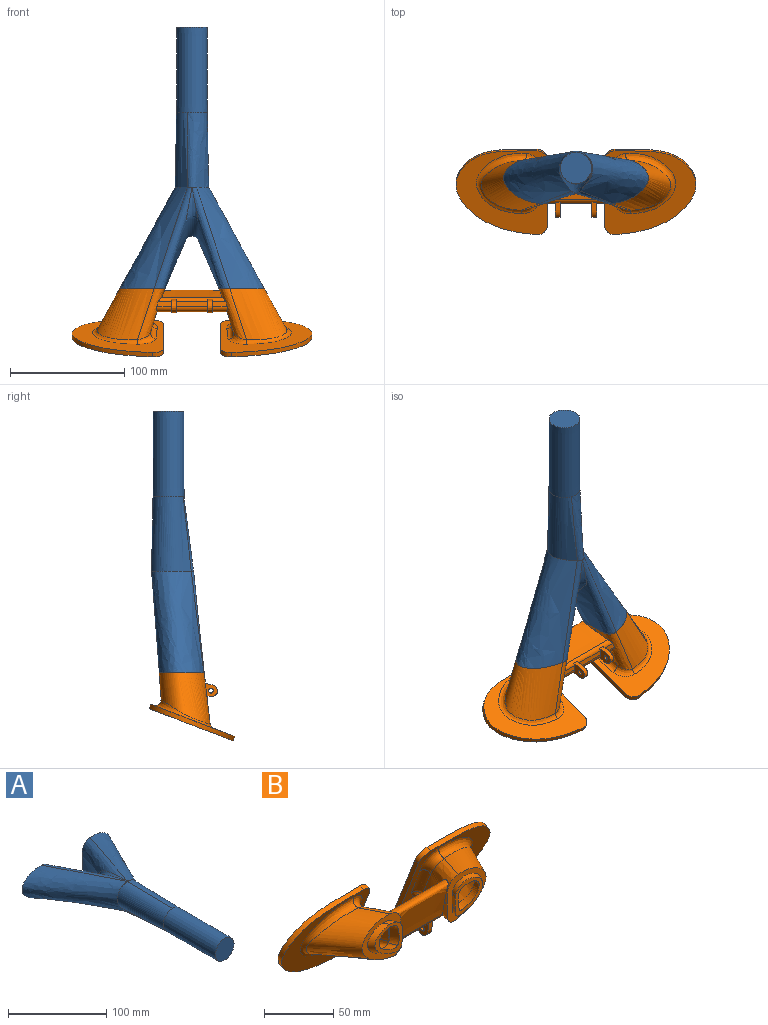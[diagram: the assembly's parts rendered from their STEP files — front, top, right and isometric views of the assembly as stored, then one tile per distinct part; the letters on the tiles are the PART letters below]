
ASSEMBLY  parts=2 mates=1
PART A: 30 faces, bbox 138.5x252.4x49 mm
  f0: bspline ~4.21x1.51mm, area 0.9mm2, adj f2,f13,f14,f15
  f1: plane 8.5x1.11mm, normal (0,-1,0), area 1.6mm2, adj f5,f14
  f2: plane 6.41x0.91mm, normal (0,-1,0), area 1.4mm2, adj f0,f5,f6,f13
  f3: plane 17.1x17.1mm, normal (0,1,0), area 229.7mm2, adj f4
  f4: cone r=5.55mm half-angle=2.5deg, axis (0,-1,0), area 3103.6mm2, adj f3,f5,f6
  f5: bspline ~65x21.5mm, area 1779.1mm2, adj f1,f2,f4,f6,f8,f10
  f6: bspline ~65x19.47mm, area 1298.2mm2, adj f2,f4,f5,f7,f9,f10
  f7: plane 8.48x1.1mm, normal (0,-1,0), area 1.6mm2, adj f6,f12
  f8: plane 4.77x4.68mm, normal (0,1,0), area 1mm2, adj f5,f14
  f9: plane 4.77x4.68mm, normal (0,1,0), area 1mm2, adj f6,f12
  f10: plane 15.72x8.94mm, normal (0,1,0), area 6.3mm2, adj f5,f6,f11,f12,f14,f15
  f11: bspline ~96.65x53.47mm, area 2584.8mm2, adj f10,f12,f13,f15,f17
  f12: bspline ~98.61x60.45mm, area 3778.7mm2, adj f7,f9,f10,f11,f13,f17
  f13: bspline ~4.27x1.64mm, area 0.9mm2, adj f0,f2,f11,f12
  f14: bspline ~98.61x60.44mm, area 3778.7mm2, adj f0,f1,f8,f10,f15,f16
  f15: bspline ~108.27x58.9mm, area 2584.8mm2, adj f0,f10,f11,f14,f16
  f16: plane 39.79x39.48mm, normal (0,1,0), area 579.5mm2, adj f14,f15,f19,f26
  f17: plane 39.77x39.46mm, normal (0,1,0), area 579.6mm2, adj f11,f12,f18,f24
  f18: bspline ~101.02x51.7mm, area 3195.4mm2, adj f17,f22,f24,f25,f29
  f19: bspline ~101.02x51.7mm, area 3193.5mm2, adj f16,f22,f26,f27,f29
  f20: plane 27.05x27.05mm, normal (0,-1,0), area 574.7mm2, adj f21
  f21: cone r=13.53mm half-angle=0deg, axis (0,1,0), area 6379.4mm2, adj f20,f22,f23
  f22: bspline ~65x37.02mm, area 3332mm2, adj f18,f19,f21,f23,f26
  f23: bspline ~65.77x34.91mm, area 2741.8mm2, adj f21,f22,f24,f27,f28
  f24: bspline ~111.93x71.83mm, area 5752.2mm2, adj f17,f18,f23,f25
  f25: cylinder r=11.3mm len=2.76mm, axis (0.37,0.92,-0.07), area 1.7mm2, adj f18,f24,f28
  f26: bspline ~101.1x66.24mm, area 5752.5mm2, adj f16,f19,f22,f27
  f27: cylinder r=11.33mm len=2.86mm, axis (0.37,-0.92,0.07), area 1.7mm2, adj f19,f23,f26,f28
  f28: bspline ~3.24x0.81mm, area 0.4mm2, adj f23,f25,f27
  f29: bspline ~46.56x37.54mm, area 612.9mm2, adj f18,f19
PART B: 80 faces, bbox 214.9x78.1x79.1 mm
  f0: plane 38.66x35.69mm, normal (0,-0.93,-0.36), area 1179.4mm2, adj f1,f2
  f1: bspline ~49.35x47.8mm, area 2433.5mm2, adj f0,f2,f71
  f2: bspline ~48.81x34.27mm, area 1258.8mm2, adj f0,f1,f70,f71,f72,f73
  f3: plane 26.69x25.63mm, normal (0,1,0), area 146.6mm2, adj f4,f70,f71,f73
  f4: bspline ~25.62x20.83mm, area 557.8mm2, adj f3,f5,f72
  f5: plane 29.75x29.28mm, normal (0,-1,0), area 261.4mm2, adj f4,f68,f69
  f6: plane 4.32x1.28mm, normal (0,1,0), area 0.7mm2, adj f12,f14
  f7: plane 38.66x35.66mm, normal (0,-0.93,-0.36), area 1178.6mm2, adj f8,f9,f15
  f8: bspline ~49.35x47.8mm, area 2433.5mm2, adj f7,f9,f11
  f9: bspline ~48.81x34.27mm, area 1258.8mm2, adj f7,f8,f11,f12,f15
  f10: plane 28.48x27.41mm, normal (0,1,0), area 74.5mm2, adj f11,f12,f13,f14
  f11: bspline ~30.27x28.42mm, area 140.7mm2, adj f8,f9,f10,f12
  f12: bspline ~24.9x17.72mm, area 121.3mm2, adj f6,f9,f10,f11,f13,f14
  f13: bspline ~24.99x23.73mm, area 473.2mm2, adj f10,f12,f14,f66
  f14: bspline ~19.22x10.5mm, area 154.8mm2, adj f6,f10,f12,f13,f66
  f15: bspline ~4.07x0.5mm, area 0mm2, adj f7,f9
  f16: cylinder r=4mm len=59.09mm, axis (-1,0,0), area 279.3mm2, adj f18,f19,f20,f21,f36,f37,f38,f39
  f17: cylinder r=4mm len=61.72mm, axis (-1,0,0), area 431.6mm2, adj f18,f19,f20,f21,f36,f37,f38,f39
  f18: plane 12.86x4.19mm, normal (0,-0.09,-1), area 51.3mm2, adj f16,f17,f20,f42
  f19: plane 12.86x4.19mm, normal (0,-0.09,-1), area 51.3mm2, adj f16,f17,f21,f39
  f20: bspline ~55.24x45.18mm, area 1346.7mm2, adj f16,f17,f18,f22,f37,f54,f55,f56
  f21: bspline ~55.24x45.18mm, area 1346.8mm2, adj f16,f17,f19,f29,f37,f53,f59,f60
  f22: bspline ~55.29x52.17mm, area 2946.7mm2, adj f20,f54,f57
  f23: cylinder r=9mm len=9.84mm, axis (0,-0.93,-0.36), area 59.6mm2, adj f24,f26,f27,f28
  f24: extruded ~74.76x70.56mm, area 712.1mm2, adj f23,f25,f27,f28
  f25: cylinder r=9mm len=9.84mm, axis (0,-0.93,-0.36), area 57.9mm2, adj f24,f26,f27,f28
  f26: plane 57.99x25.44mm, normal (1,0,0), area 242.3mm2, adj f23,f25,f27,f28
  f27: plane 80.61x73.97mm, normal (0,0.93,0.36), area 5149.4mm2, adj f23,f24,f25,f26
  f28: plane 80.61x73.97mm, normal (0,-0.93,-0.36), area 2566.2mm2, adj f23,f24,f25,f26,f55,f56,f57,f58
  f29: bspline ~62.5x55.41mm, area 2946.7mm2, adj f21,f53,f61
  f30: cylinder r=9mm len=9.84mm, axis (0,-0.93,-0.36), area 59.6mm2, adj f31,f33,f34,f35
  f31: plane 57.99x25.44mm, normal (-1,0,0), area 242.3mm2, adj f30,f32,f34,f35
  f32: cylinder r=9mm len=9.84mm, axis (0,-0.93,-0.36), area 57.9mm2, adj f31,f33,f34,f35
  f33: extruded ~74.76x70.56mm, area 712.1mm2, adj f30,f32,f34,f35
  f34: plane 80.61x73.97mm, normal (0,0.93,0.36), area 5149.4mm2, adj f30,f31,f32,f33
  f35: plane 80.61x73.97mm, normal (0,-0.93,-0.36), area 2566.3mm2, adj f30,f31,f32,f33,f59,f60,f61,f62
  f36: plane 28x4.19mm, normal (0,-0.09,-1), area 117.7mm2, adj f16,f17,f40,f43
  f37: extruded ~60.88x30.5mm, area 3844.7mm2, adj f16,f17,f20,f21
  f38: extruded ~13.81x11.49mm, area 132.6mm2, adj f16,f17,f39,f40
  f39: plane 14.91x12.15mm, normal (1,0,0), area 81.5mm2, adj f16,f17,f19,f38,f44,f45,f46,f47
  f40: plane 14.91x12.15mm, normal (-1,0,0), area 106.1mm2, adj f16,f17,f36,f38,f51
  f41: extruded ~13.81x11.49mm, area 132.6mm2, adj f16,f17,f42,f43
  f42: plane 14.91x12.15mm, normal (-1,0,0), area 106.1mm2, adj f16,f17,f18,f41,f52
  f43: plane 14.91x12.15mm, normal (1,0,0), area 106.1mm2, adj f16,f17,f36,f41,f52
  f44: plane 3.61x2mm, normal (0,0.29,-0.96), area 7.6mm2, adj f39,f45,f49,f50
  f45: plane 2.77x2.57mm, normal (0,-0.68,-0.73), area 7.6mm2, adj f39,f44,f46,f50
  f46: plane 3.69x2mm, normal (0,-0.97,0.22), area 7.6mm2, adj f39,f45,f47,f50
  f47: plane 3.61x2mm, normal (0,-0.29,0.96), area 7.6mm2, adj f39,f46,f48,f50
  f48: plane 2.77x2.57mm, normal (0,0.68,0.73), area 7.6mm2, adj f39,f47,f49,f50
  f49: plane 3.69x2mm, normal (0,0.97,-0.22), area 7.6mm2, adj f39,f44,f48,f50
  f50: plane 7.37x7.23mm, normal (1,0,0), area 24.6mm2, adj f44,f45,f46,f47,f48,f49,f51
  f51: cylinder r=2mm len=4mm, axis (1,0,0), area 25.1mm2, adj f40,f50
  f52: cylinder r=2mm len=4mm, axis (1,0,0), area 50.3mm2, adj f42,f43
  f53: plane 43.48x43.17mm, normal (0,-1,0), area 583.6mm2, adj f21,f29,f68,f69
  f54: plane 43.46x43.15mm, normal (0,-1,0), area 579.5mm2, adj f20,f22,f63,f64,f65
  f55: bspline ~20.03x13.96mm, area 201mm2, adj f20,f28,f56,f57
  f56: bspline ~25.01x15.63mm, area 239.1mm2, adj f20,f28,f55,f58
  f57: bspline ~52.75x43.97mm, area 671.3mm2, adj f20,f22,f28,f55,f58
  f58: bspline ~16.96x14.31mm, area 131.6mm2, adj f20,f28,f56,f57
  f59: bspline ~20.03x13.96mm, area 202.1mm2, adj f21,f35,f60,f61
  f60: bspline ~25.7x16.08mm, area 247.7mm2, adj f21,f35,f59,f62
  f61: bspline ~52.75x43.97mm, area 671.3mm2, adj f21,f29,f35,f59,f62
  f62: bspline ~16.64x13.51mm, area 121.2mm2, adj f21,f35,f60,f61
  f63: bspline ~15.44x11mm, area 99mm2, adj f54,f64,f65,f66
  f64: bspline ~30.89x28.78mm, area 321.5mm2, adj f54,f63,f65,f66
  f65: bspline ~11.6x5mm, area 59.3mm2, adj f54,f63,f64,f66
  f66: plane 28.69x28.28mm, normal (0,-1,0), area 266.4mm2, adj f13,f14,f63,f64,f65
  f67: cylinder r=31.58mm len=1.16mm, axis (0,-1,0), area 0mm2, adj f21
  f68: bspline ~12.56x5.5mm, area 64.2mm2, adj f5,f53,f69
  f69: bspline ~30.81x28.47mm, area 416.9mm2, adj f5,f53,f68
  f70: bspline ~10.95x2.94mm, area 33.3mm2, adj f2,f3,f71,f72
  f71: bspline ~30.27x28.41mm, area 140.7mm2, adj f1,f2,f3,f70,f73
  f72: bspline ~4.09x2.92mm, area 8.8mm2, adj f2,f4,f70,f73
  f73: bspline ~17.81x15.08mm, area 85.2mm2, adj f2,f3,f71,f72
  f74: cylinder r=1mm len=58.97mm, axis (-1,0,0), area 119.5mm2, adj f75,f77,f78,f79
  f75: plane 58.46x4.63mm, normal (0,0.16,0.99), area 266.8mm2, adj f74,f76,f78,f79
  f76: cylinder r=1mm len=55.43mm, axis (-1,0,0), area 48.1mm2, adj f75,f77,f78,f79
  f77: extruded ~58.97x25.38mm, area 3199.2mm2, adj f74,f76,f78,f79
  f78: bspline ~30.27x18.49mm, area 172.1mm2, adj f74,f75,f76,f77
  f79: bspline ~30.27x18.49mm, area 172.1mm2, adj f74,f75,f76,f77
PLACE A rot(axis=(-1,0,0),90deg) t=(6.25,79.24,164.69)mm
PLACE B rot(axis=(-1,0,0),90deg) t=(6.25,79.23,164.69)mm
MATE fastened A.f16 <-> B.f53  axis (0,0,-1) through (30.01,67.63,10.69)mm
